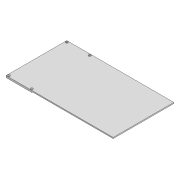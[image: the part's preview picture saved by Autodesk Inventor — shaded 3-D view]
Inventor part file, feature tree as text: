
AUTODESK INVENTOR PART (.ipt)
format: ipt  version: 2021 (Build 250183000, 183)  size: 111,616 bytes
history: native  units: mm
features: sketch x3, extrude x2, other x1, hole x1, fillet x1, projected_geometry x1
ambient origin geometry x8: Origin, YZ Plane, XZ Plane, XY Plane, X Axis, Y Axis, Z Axis, Center Point
bodies: Body1 (feature_tree)
feature tree (9):
  other  "Твердое тело1"
  extrude  "Выдавливание1"  Depth=170.0mm
  extrude  "Выдавливание3"  Depth=300.0mm
  hole  "Отверстие1"  [1 undecoded]
  fillet  "Сопряжение1"  Radius=162.0mm
  sketch  "Эскиз1"
  sketch  "Эскиз2"
  sketch  "Эскиз4"
  projected_geometry  "Спроецированная петля2"
note: 1 required parameter value undecoded (feature->parameter linkage not recoverable at this tier; creation-order binding heuristic only, values carry confidence <= 0.55)
